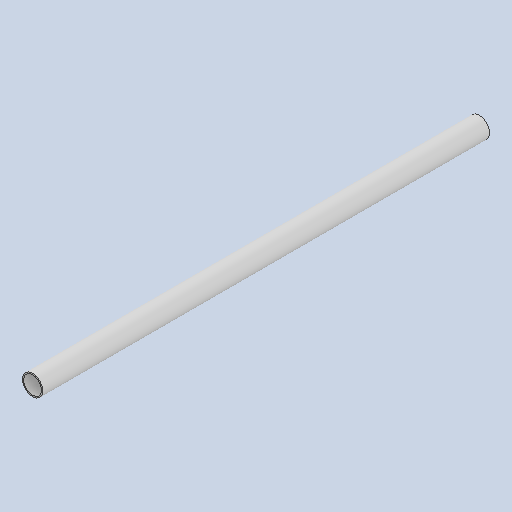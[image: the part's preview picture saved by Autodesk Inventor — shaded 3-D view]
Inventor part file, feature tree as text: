
AUTODESK INVENTOR PART (.ipt)
format: ipt  version: 2024.2 (Build 282272000, 272)  size: 240,640 bytes
history: native  units: mm
features: extrude x1
ambient origin geometry x8: Origin, YZ Plane, XZ Plane, XY Plane, X Axis, Y Axis, Z Axis, Center Point
bodies: Solid1 (feature_tree)
feature tree (1):
  extrude  "Extrusion1"  Depth=2.0mm
